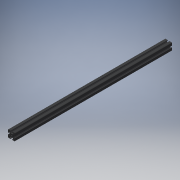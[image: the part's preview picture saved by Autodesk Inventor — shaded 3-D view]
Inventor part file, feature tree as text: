
AUTODESK INVENTOR PART (.ipt)
format: ipt  version: 2019 (Build 230136000, 136)  size: 231,936 bytes
history: native  units: in
note: dims shown in document units (in); Inventor stores cm internally (conversion verified against a paired STEP export)
features: plane x1, extrude x1, sketch x1
ambient origin geometry x8: Origin, YZ Plane, XZ Plane, XY Plane, X Axis, Y Axis, Z Axis, Center Point
bodies: Solid1 (feature_tree)
feature tree (3):
  plane  "Work Plane1"
  extrude  "Extrusion1"  [1 undecoded]
  sketch  "Sketch1"  dims[d0=12.0in d1=0.0in]
note: 1 required parameter value undecoded (feature->parameter linkage not recoverable at this tier; creation-order binding heuristic only, values carry confidence <= 0.55)
